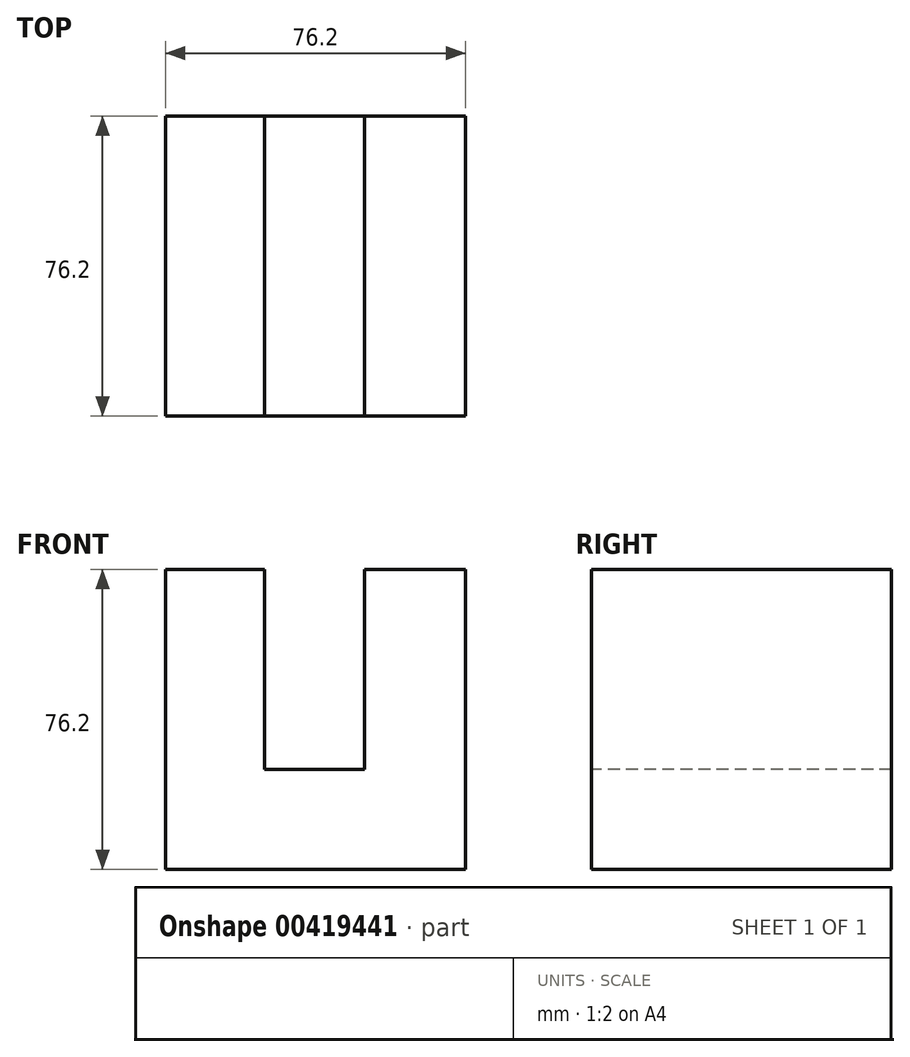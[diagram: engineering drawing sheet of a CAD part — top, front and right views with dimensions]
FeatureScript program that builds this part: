
annotation { "Feature Type Name" : "Feature", "Feature Type Description" : "" }
export const myFeature = defineFeature(function(context is Context, id is Id, definition is map)
    precondition{}
    {
        {
            var Q0;
            Q0=qCreatedBy(makeId("Front.planeOp"),FACE);
            var sketch = newSketch(context, id + "F0", { "sketchPlane" : qUnion([Q0])});
            skLineSegment(sketch, "E0.bottom", {"start": v(38.1, -38.1) * mm, "end": v(-38.1, -38.1) * mm});
            skLineSegment(sketch, "E0.top", {"start": v(38.1, 38.1) * mm, "end": v(-38.1, 38.1) * mm});
            skLineSegment(sketch, "E0.left", {"start": v(38.1, -38.1) * mm, "end": v(38.1, 38.1) * mm});
            skLineSegment(sketch, "E0.right", {"start": v(-38.1, -38.1) * mm, "end": v(-38.1, 38.1) * mm});
            skPoint(sketch, "E0.middle", {"position": v(0, 0) * mm});
            skSolve(sketch);
        }
        {
            var Q0;
            Q0 = qSketchRegion(id + "F0", true);
            extrude(context, id + "F1", {"entities" : qUnion([Q0]), "depth" : 76.2 * mm});
        }
        {
            var Q0;
            Q0=makeQuery(id+"F1.opExtrude","CAP_FACE",FACE,{"disambiguationData":[OSD([sQuery(id+"F0.wireOp",EDGE,"E0.bottom"),sQuery(id+"F0.wireOp",EDGE,"E0.top"),sQuery(id+"F0.wireOp",EDGE,"E0.left"),sQuery(id+"F0.wireOp",EDGE,"E0.right")])],"isStart":false});
            var sketch = newSketch(context, id + "F2", { "sketchPlane" : qUnion([Q0])});
            skLineSegment(sketch, "E1", {"start": v(-13, 38.1) * mm, "end": v(-13, -12.7) * mm});
            skLineSegment(sketch, "E2", {"start": v(-13, -12.7) * mm, "end": v(12.4, -12.7) * mm});
            skLineSegment(sketch, "E3", {"start": v(12.4, -12.7) * mm, "end": v(12.4, 38.1) * mm});
            skLineSegment(sketch, "E4", {"start": v(12.4, 38.1) * mm, "end": v(-13, 38.1) * mm});
            skSolve(sketch);
        }
        {
            var Q0;
            Q0 = qSketchRegion(id + "F2", true);
            extrude(context, id + "F3", {"entities" : qUnion([Q0]), "operationType" : NewBodyOperationType.REMOVE, "oppositeDirection" : true, "depth" : 262.13 * mm});
        }
    });
